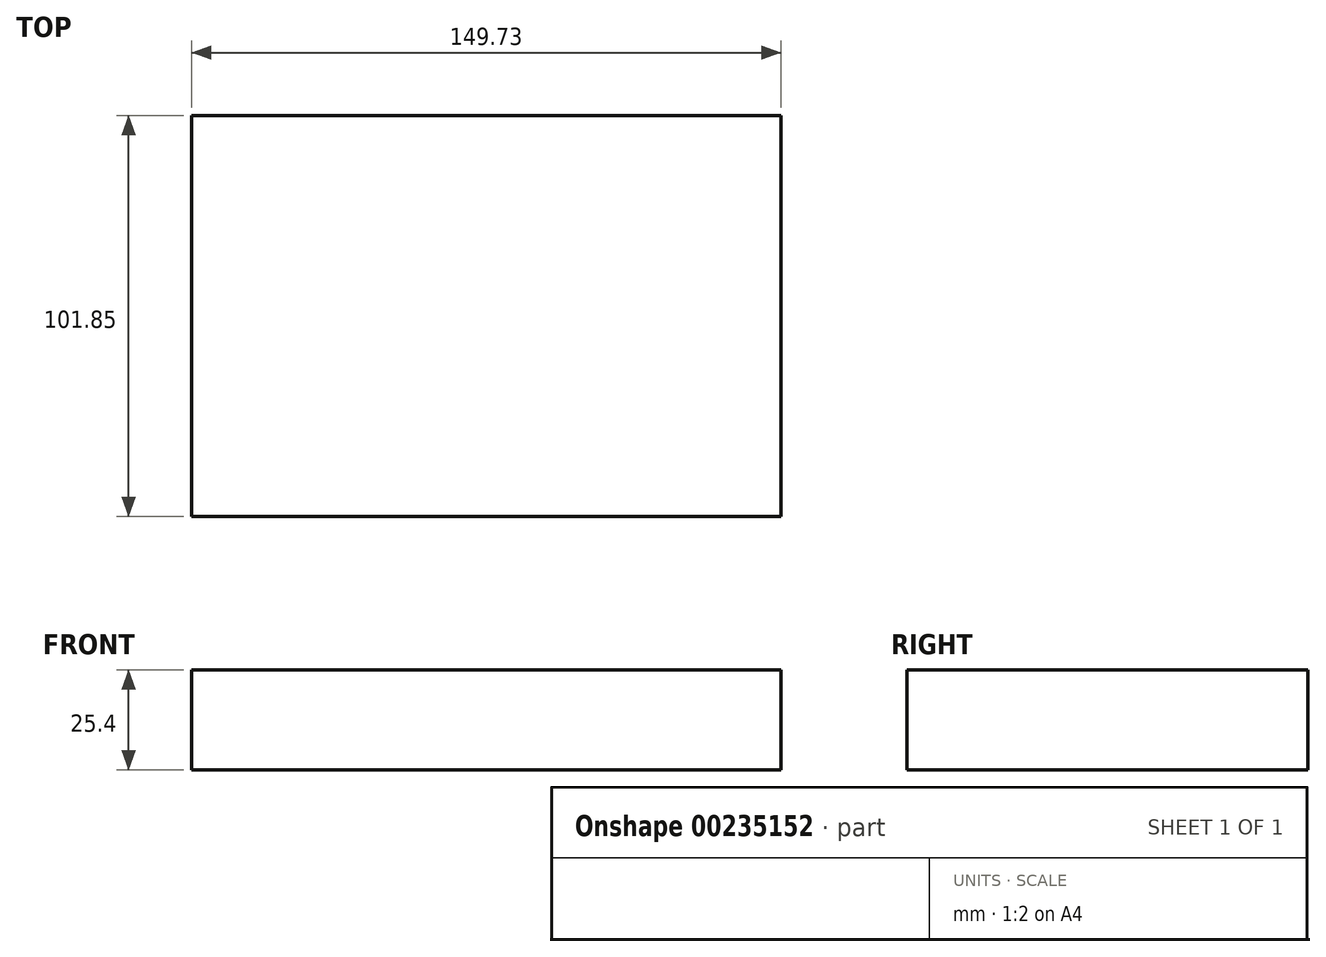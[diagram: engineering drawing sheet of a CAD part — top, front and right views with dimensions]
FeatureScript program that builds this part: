
annotation { "Feature Type Name" : "Feature", "Feature Type Description" : "" }
export const myFeature = defineFeature(function(context is Context, id is Id, definition is map)
    precondition{}
    {
        {
            var Q0;
            Q0=qCreatedBy(makeId("Top.planeOp"),FACE);
            var sketch = newSketch(context, id + "F0", { "sketchPlane" : qUnion([Q0])});
            skLineSegment(sketch, "E0.bottom", {"start": v(-87.1, 53.01) * mm, "end": v(62.63, 53.01) * mm});
            skLineSegment(sketch, "E0.top", {"start": v(-87.1, -48.84) * mm, "end": v(62.63, -48.84) * mm});
            skLineSegment(sketch, "E0.left", {"start": v(-87.1, 53.01) * mm, "end": v(-87.1, -48.84) * mm});
            skLineSegment(sketch, "E0.right", {"start": v(62.63, 53.01) * mm, "end": v(62.63, -48.84) * mm});
            skSolve(sketch);
        }
        {
            var Q0;
            Q0 = qSketchRegion(id + "F0", true);
            extrude(context, id + "F1", {"entities" : qUnion([Q0]), "depth" : 25.4 * mm});
        }
    });
